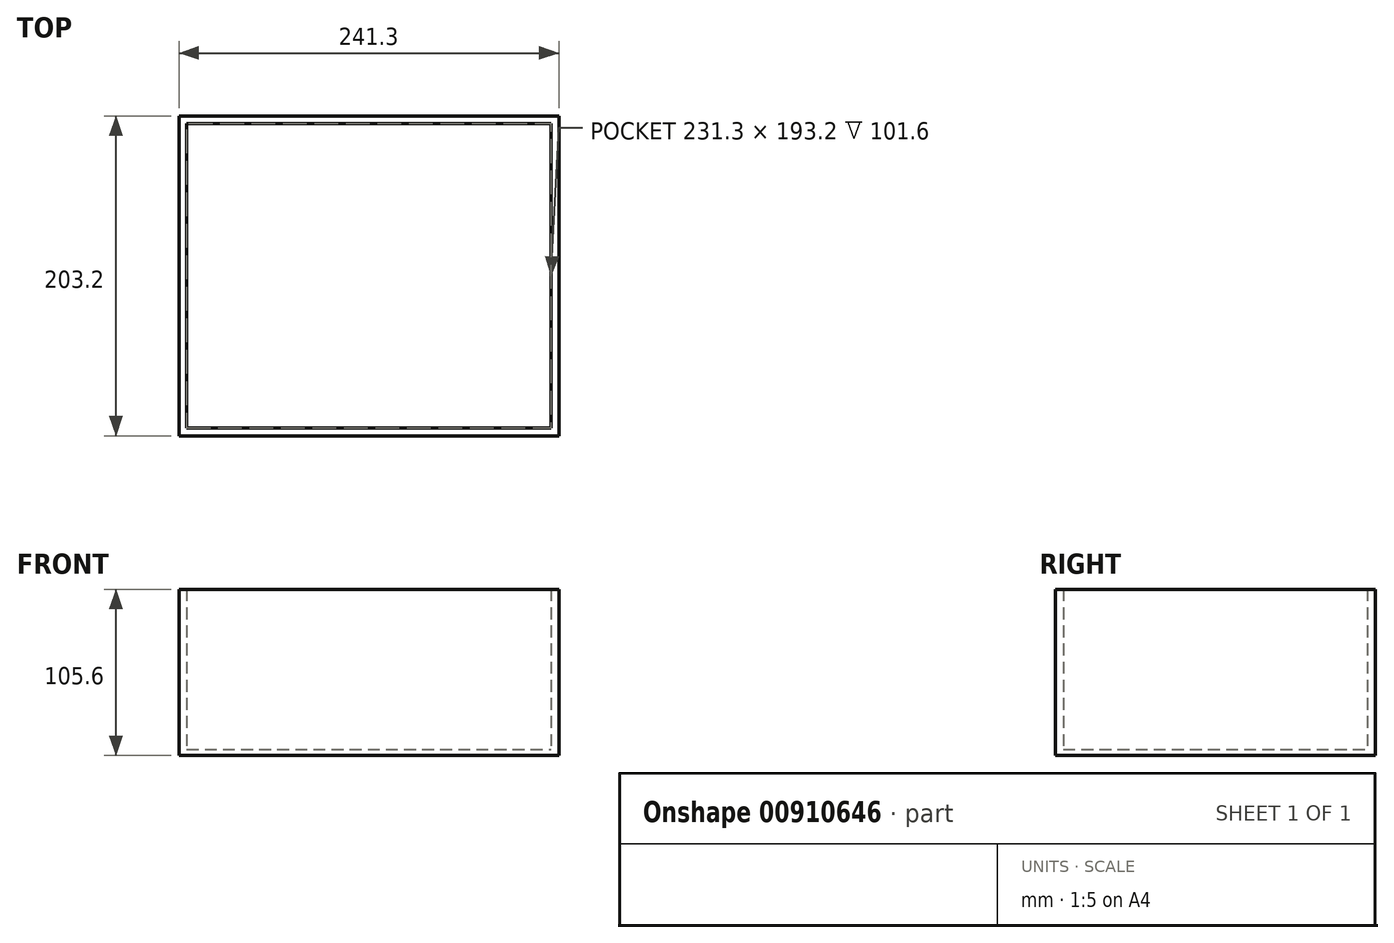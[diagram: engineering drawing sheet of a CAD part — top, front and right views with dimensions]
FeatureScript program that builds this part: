
annotation { "Feature Type Name" : "Feature", "Feature Type Description" : "" }
export const myFeature = defineFeature(function(context is Context, id is Id, definition is map)
    precondition{}
    {
        {
            var Q0;
            Q0=qCreatedBy(makeId("Top.planeOp"),FACE);
            var sketch = newSketch(context, id + "F0", { "sketchPlane" : qUnion([Q0])});
            skLineSegment(sketch, "E0.bottom", {"start": v(120.65, -110.73) * mm, "end": v(-120.65, -110.73) * mm});
            skLineSegment(sketch, "E0.top", {"start": v(120.65, 92.47) * mm, "end": v(-120.65, 92.47) * mm});
            skLineSegment(sketch, "E0.left", {"start": v(120.65, -110.73) * mm, "end": v(120.65, 92.47) * mm});
            skLineSegment(sketch, "E0.right", {"start": v(-120.65, -110.73) * mm, "end": v(-120.65, 92.47) * mm});
            skPoint(sketch, "E0.middle", {"position": v(0, -9.13) * mm});
            skSolve(sketch);
        }
        {
            var Q0;
            Q0=makeQuery(id+"F0.imprint","IMPRINT",FACE,{"disambiguationData":[TD([[makeQuery(id+"F0.imprint","IMPRINT",EDGE,{"derivedFrom":sQuery(id+"F0.wireOp",EDGE,"E0.bottom")}),-1.0]])]});
            extrude(context, id + "F1", {"entities" : qUnion([Q0]), "depth" : 4 * mm, "offsetDistance" : 25 * mm});
        }
        {
            var Q0;
            Q0=makeQuery(id+"F1.opExtrude","CAP_FACE",FACE,{"disambiguationData":[OSD([sQuery(id+"F0.wireOp",EDGE,"E0.bottom"),sQuery(id+"F0.wireOp",EDGE,"E0.top"),sQuery(id+"F0.wireOp",EDGE,"E0.left"),sQuery(id+"F0.wireOp",EDGE,"E0.right")])],"isStart":false});
            var sketch = newSketch(context, id + "F2", { "sketchPlane" : qUnion([Q0])});
            skLineSegment(sketch, "E1", {"start": v(-120.65, 92.47) * mm, "end": v(-120.65, -110.73) * mm});
            skLineSegment(sketch, "E2", {"start": v(-120.65, -110.73) * mm, "end": v(120.65, -110.73) * mm});
            skLineSegment(sketch, "E3", {"start": v(120.65, -110.73) * mm, "end": v(120.65, 92.47) * mm});
            skLineSegment(sketch, "E4.bottom", {"start": v(-115.65, -105.73) * mm, "end": v(115.65, -105.73) * mm});
            skLineSegment(sketch, "E4.top", {"start": v(-115.65, 87.47) * mm, "end": v(115.65, 87.47) * mm});
            skLineSegment(sketch, "E4.left", {"start": v(-115.65, -105.73) * mm, "end": v(-115.65, 87.47) * mm});
            skLineSegment(sketch, "E4.right", {"start": v(115.65, -105.73) * mm, "end": v(115.65, 87.47) * mm});
            skSolve(sketch);
        }
        {
            var Q0;
            Q0=makeQuery(id+"F2.imprint","IMPRINT",FACE,{"disambiguationData":[TD([[makeQuery(id+"F2.imprint","IMPRINT",EDGE,{"derivedFrom":sQuery(id+"F2.wireOp",EDGE,"E1")}),-1.0]])]});
            extrude(context, id + "F3", {"entities" : qUnion([Q0]), "operationType" : NewBodyOperationType.ADD, "depth" : 101.6 * mm, "offsetDistance" : 25 * mm});
        }
    });
